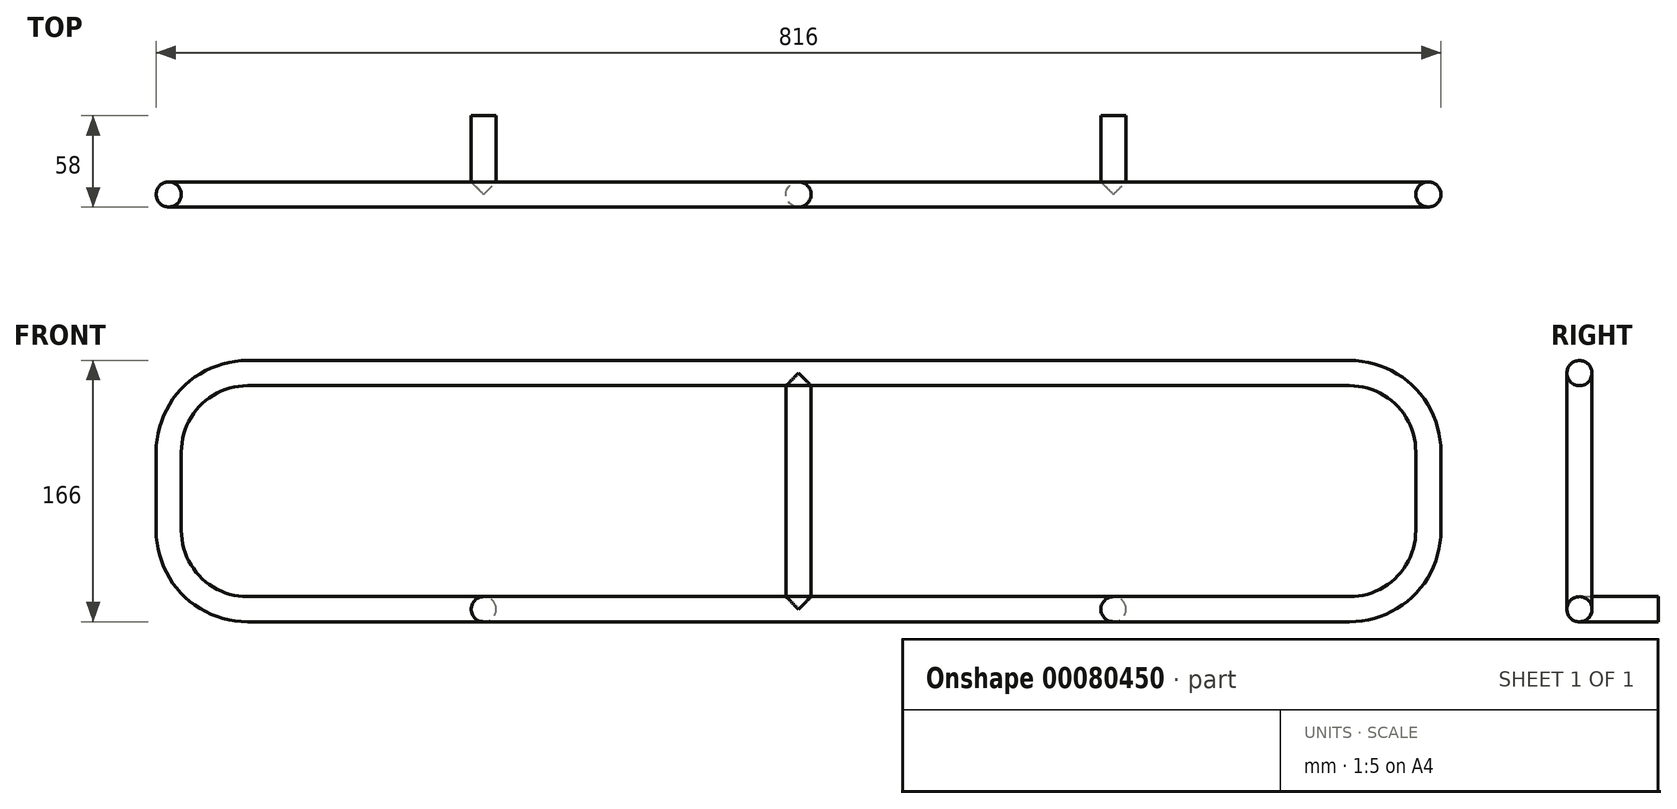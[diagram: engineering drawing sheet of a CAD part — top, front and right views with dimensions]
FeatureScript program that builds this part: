
annotation { "Feature Type Name" : "Feature", "Feature Type Description" : "" }
export const myFeature = defineFeature(function(context is Context, id is Id, definition is map)
    precondition{}
    {
        {
            var Q0;
            Q0=qCreatedBy(makeId("Front.planeOp"),FACE);
            var sketch = newSketch(context, id + "F0", { "sketchPlane" : qUnion([Q0])});
            skLineSegment(sketch, "E0.bottom", {"start": v(-350, 0) * mm, "end": v(350, 0) * mm});
            skLineSegment(sketch, "E0.top", {"start": v(-350, 150) * mm, "end": v(350, 150) * mm});
            skLineSegment(sketch, "E0.left", {"start": v(-400, 50) * mm, "end": v(-400, 100) * mm});
            skLineSegment(sketch, "E0.right", {"start": v(400, 50) * mm, "end": v(400, 100) * mm});
            skPoint(sketch, "E1.visualSharp", {"position": v(-400, 150) * mm});
            skArc(sketch, "E1.filletArc", {"start": v(-350, 150) * mm, "mid": v(-385.36, 135.36) * mm, "end": v(-400, 100) * mm});
            skPoint(sketch, "E2.visualSharp", {"position": v(-400, 0) * mm});
            skArc(sketch, "E2.filletArc", {"start": v(-400, 50) * mm, "mid": v(-385.36, 14.64) * mm, "end": v(-350, 0) * mm});
            skPoint(sketch, "E3.visualSharp", {"position": v(400, 150) * mm});
            skArc(sketch, "E3.filletArc", {"start": v(400, 100) * mm, "mid": v(385.36, 135.36) * mm, "end": v(350, 150) * mm});
            skPoint(sketch, "E4.visualSharp", {"position": v(400, 0) * mm});
            skArc(sketch, "E4.filletArc", {"start": v(350, 0) * mm, "mid": v(385.36, 14.64) * mm, "end": v(400, 50) * mm});
            skSolve(sketch);
        }
        {
            var Q0;
            Q0=qCreatedBy(makeId("Right.planeOp"),FACE);
            var Q1;
            Q1=sQuery(id+"F0.wireOp",VERTEX,"E2.filletArc.end");
            cPlane(context, id + "F1", {"entities" : qUnion([Q0, Q1]), "cplaneType" : CPlaneType.PLANE_POINT, "offset" : 150 * mm, "width" : 150 * mm, "height" : 150 * mm});
        }
        {
            var Q0;
            Q0=qCreatedBy(id+"F1.planeOp",FACE);
            var sketch = newSketch(context, id + "F2", { "sketchPlane" : qUnion([Q0])});
            skCircle(sketch, "E5", {"center": v(0, 0) * mm, "radius": 8 * mm});
            skSolve(sketch);
        }
        {
            var Q0;
            Q0=makeQuery(id+"F2.imprint","IMPRINT",FACE,{"disambiguationData":[TD([[makeQuery(id+"F2.imprint","IMPRINT",EDGE,{"derivedFrom":sQuery(id+"F2.wireOp",EDGE,"E5")}),1.0]])]});
            var Q1;
            Q1=sQuery(id+"F0.wireOp",EDGE,"E0.bottom");
            var Q2;
            Q2=sQuery(id+"F0.wireOp",EDGE,"E4.filletArc");
            var Q3;
            Q3=sQuery(id+"F0.wireOp",EDGE,"E0.right");
            var Q4;
            Q4=sQuery(id+"F0.wireOp",EDGE,"E3.filletArc");
            var Q5;
            Q5=sQuery(id+"F0.wireOp",EDGE,"E0.top");
            var Q6;
            Q6=sQuery(id+"F0.wireOp",EDGE,"E1.filletArc");
            var Q7;
            Q7=sQuery(id+"F0.wireOp",EDGE,"E0.left");
            var Q8;
            Q8=sQuery(id+"F0.wireOp",EDGE,"E2.filletArc");
            sweep(context, id + "F3", {"profiles" : qUnion([Q0]), "path" : qUnion([Q1, Q2, Q3, Q4, Q5, Q6, Q7, Q8])});
        }
        {
            var Q0;
            Q0=qCreatedBy(makeId("Top.planeOp"),FACE);
            cPlane(context, id + "F4", {"entities" : qUnion([Q0]), "cplaneType" : CPlaneType.OFFSET, "offset" : 50 * mm, "width" : 150 * mm, "height" : 150 * mm});
        }
        {
            var Q0;
            Q0=qCreatedBy(id+"F4.planeOp",FACE);
            var sketch = newSketch(context, id + "F5", { "sketchPlane" : qUnion([Q0])});
            skCircle(sketch, "E6", {"center": v(0, 0) * mm, "radius": 8 * mm});
            skSolve(sketch);
        }
        {
            var Q0;
            Q0 = qSketchRegion(id + "F5", true);
            var Q1;
            Q1=makeQuery(id+"F3.opSweep","SWEPT_FACE",FACE,{"disambiguationData":[OSD([sQuery(id+"F0.wireOp",EDGE,"E0.top"),sQuery(id+"F2.wireOp",EDGE,"E5")])]});
            var Q2;
            Q2=makeQuery(id+"F3.opSweep","SWEPT_FACE",FACE,{"disambiguationData":[OSD([sQuery(id+"F0.wireOp",EDGE,"E0.bottom"),sQuery(id+"F2.wireOp",EDGE,"E5")])]});
            extrude(context, id + "F6", {"entities" : qUnion([Q0]), "endBound" : BoundingType.UP_TO_SURFACE, "endBoundEntityFace" : qUnion([Q1]), "depth" : 25 * mm, "hasSecondDirection" : true, "secondDirectionBound" : BoundingType.UP_TO_SURFACE, "secondDirectionOppositeDirection" : true, "secondDirectionBoundEntityFace" : qUnion([Q2]), "secondDirectionDepth" : 25 * mm});
        }
        {
            var Q0;
            Q0=qCreatedBy(makeId("Front.planeOp"),FACE);
            cPlane(context, id + "F7", {"entities" : qUnion([Q0]), "cplaneType" : CPlaneType.OFFSET, "offset" : 50 * mm, "oppositeDirection" : true, "width" : 150 * mm, "height" : 150 * mm});
        }
        {
            var Q0;
            Q0=qCreatedBy(id+"F7.planeOp",FACE);
            var sketch = newSketch(context, id + "F8", { "sketchPlane" : qUnion([Q0])});
            skCircle(sketch, "E7", {"center": v(200, 0) * mm, "radius": 8 * mm});
            skCircle(sketch, "E8", {"center": v(-200, 0) * mm, "radius": 8 * mm});
            skLineSegment(sketch, "E9", {"start": v(0, 0) * mm, "end": v(0, 89) * mm, "construction": true});
            skSolve(sketch);
        }
        {
            var Q0;
            Q0 = qSketchRegion(id + "F8", true);
            var Q1;
            Q1=makeQuery(id+"F3.opSweep","SWEPT_FACE",FACE,{"disambiguationData":[OSD([sQuery(id+"F0.wireOp",EDGE,"E0.bottom"),sQuery(id+"F2.wireOp",EDGE,"E5")])]});
            extrude(context, id + "F9", {"entities" : qUnion([Q0]), "endBound" : BoundingType.UP_TO_SURFACE, "endBoundEntityFace" : qUnion([Q1]), "depth" : 25 * mm});
        }
    });
